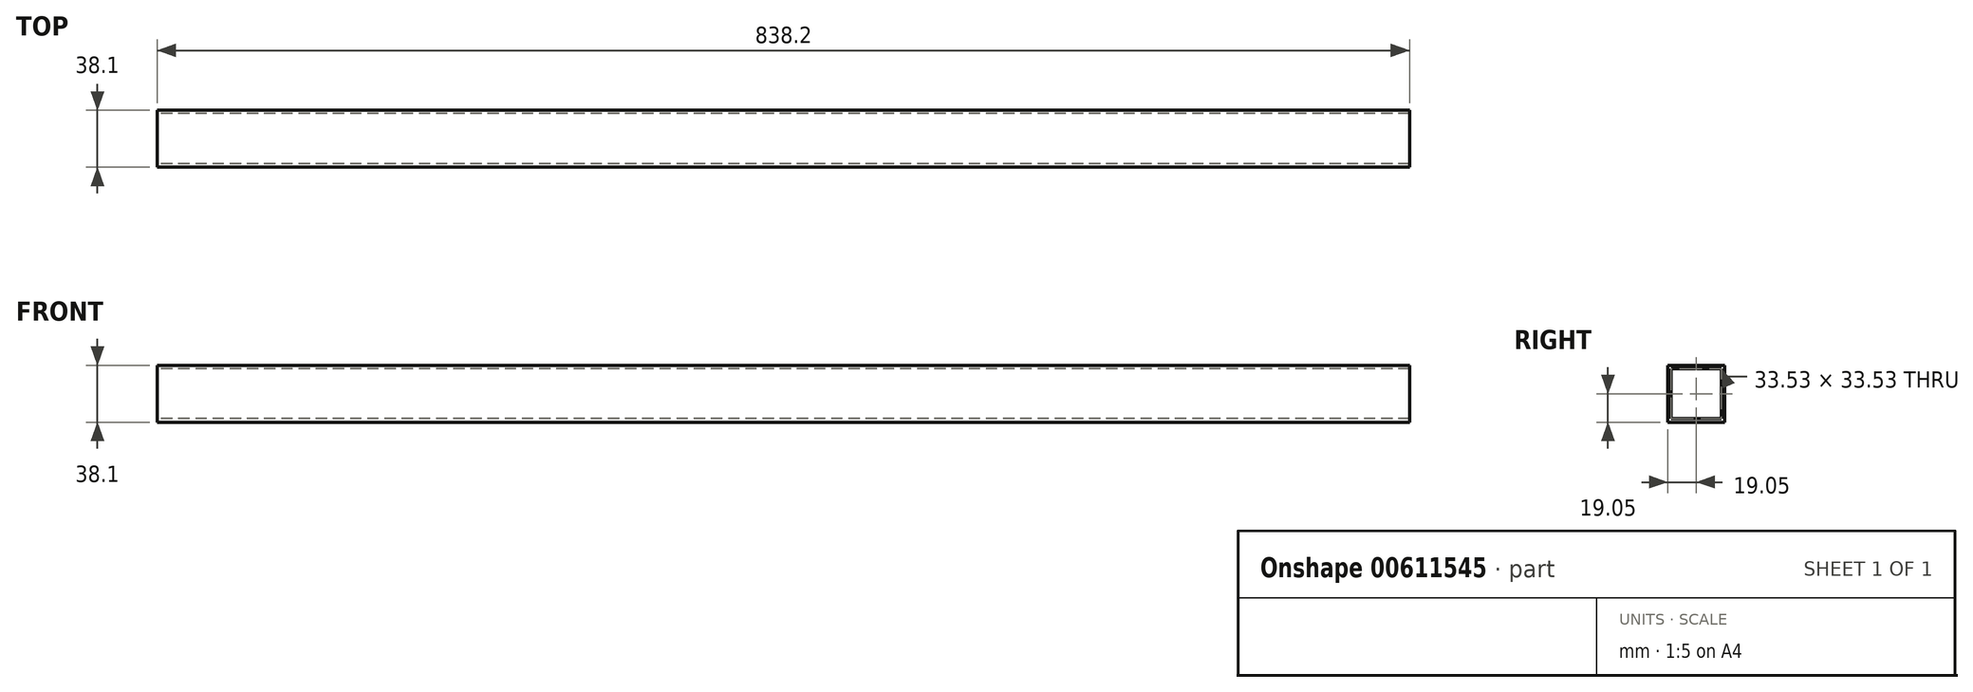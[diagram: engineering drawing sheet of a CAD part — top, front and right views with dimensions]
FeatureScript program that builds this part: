
annotation { "Feature Type Name" : "Feature", "Feature Type Description" : "" }
export const myFeature = defineFeature(function(context is Context, id is Id, definition is map)
    precondition{}
    {
        {
            var Q0;
            Q0=qCreatedBy(makeId("Right.planeOp"),FACE);
            var sketch = newSketch(context, id + "F0", { "sketchPlane" : qUnion([Q0])});
            skLineSegment(sketch, "E0.bottom", {"start": v(0, 0) * mm, "end": v(-38.1, 0) * mm});
            skLineSegment(sketch, "E0.top", {"start": v(0, -38.1) * mm, "end": v(-38.1, -38.1) * mm});
            skLineSegment(sketch, "E0.left", {"start": v(0, 0) * mm, "end": v(0, -38.1) * mm});
            skLineSegment(sketch, "E0.right", {"start": v(-38.1, 0) * mm, "end": v(-38.1, -38.1) * mm});
            skLineSegment(sketch, "E1.bottom", {"start": v(-35.81, -2.29) * mm, "end": v(-2.29, -2.29) * mm});
            skLineSegment(sketch, "E1.top", {"start": v(-35.81, -35.81) * mm, "end": v(-2.29, -35.81) * mm});
            skLineSegment(sketch, "E1.left", {"start": v(-35.81, -2.29) * mm, "end": v(-35.81, -35.81) * mm});
            skLineSegment(sketch, "E1.right", {"start": v(-2.29, -2.29) * mm, "end": v(-2.29, -35.81) * mm});
            skSolve(sketch);
        }
        {
            var Q0;
            Q0 = qSketchRegion(id + "F0", true);
            extrude(context, id + "F1", {"entities" : qUnion([Q0]), "depth" : 838.2 * mm, "offsetDistance" : 25.4 * mm});
        }
    });
